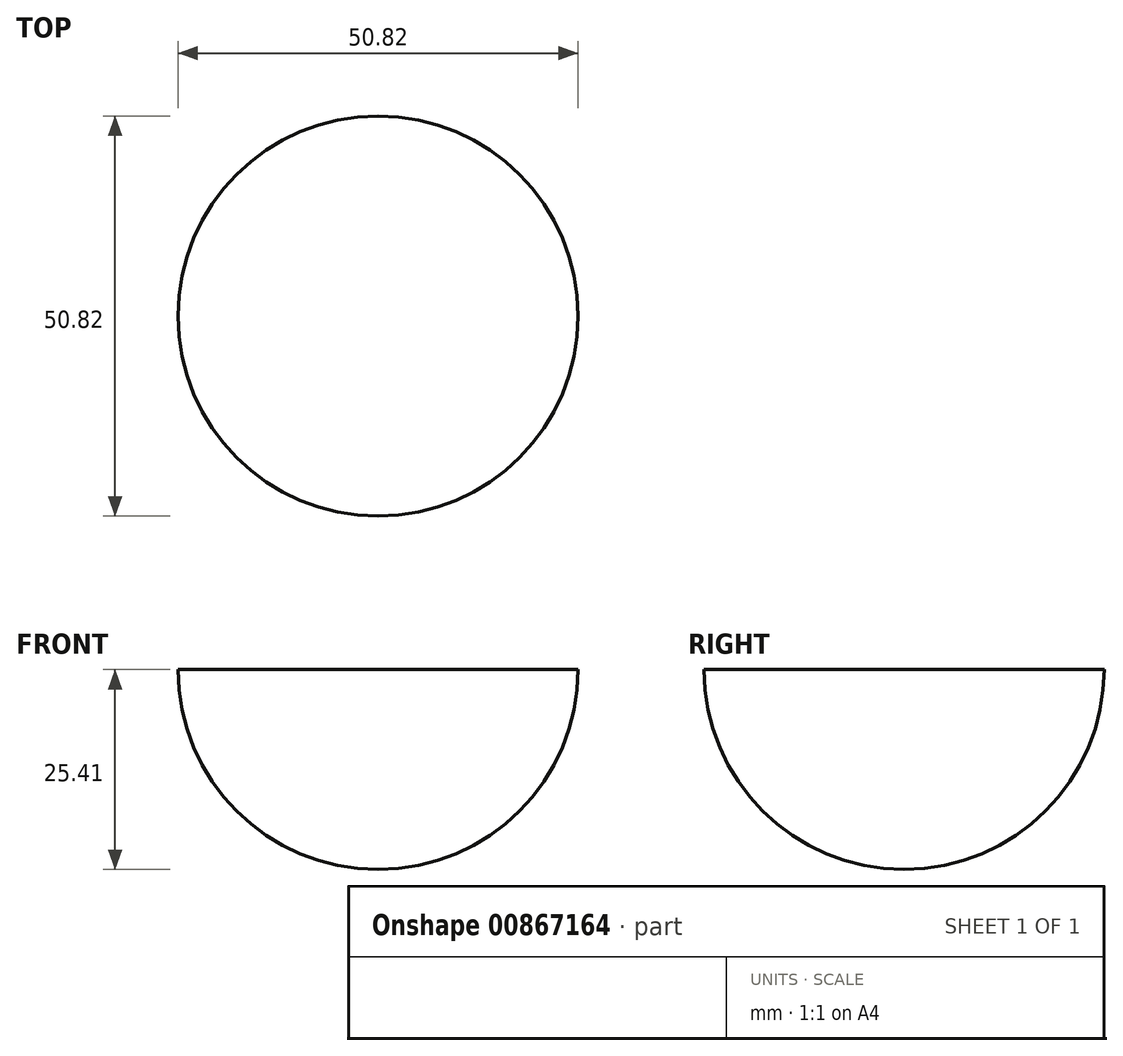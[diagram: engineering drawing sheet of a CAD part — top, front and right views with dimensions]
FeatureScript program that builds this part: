
annotation { "Feature Type Name" : "Feature", "Feature Type Description" : "" }
export const myFeature = defineFeature(function(context is Context, id is Id, definition is map)
    precondition{}
    {
        {
            var Q0;
            Q0=qCreatedBy(makeId("Top.planeOp"),FACE);
            var sketch = newSketch(context, id + "F0", { "sketchPlane" : qUnion([Q0])});
            skArc(sketch, "E0", {"start": v(0, -25.41) * mm, "mid": v(25.41, 0) * mm, "end": v(0, 25.41) * mm});
            skSolve(sketch);
        }
        {
            var Q0;
            Q0=qCreatedBy(makeId("Top.planeOp"),FACE);
            var sketch = newSketch(context, id + "F1", { "sketchPlane" : qUnion([Q0])});
            skLineSegment(sketch, "E1", {"start": v(0, 25.34) * mm, "end": v(0, 0) * mm});
            skSolve(sketch);
        }
        {
            var Q0;
            Q0=sQuery(id+"F0.wireOp",EDGE,"E0");
            var Q1;
            Q1=sQuery(id+"F1.wireOp",EDGE,"E1");
            revolve(context, id + "F2", {"bodyType" : ToolBodyType.SURFACE, "surfaceOperationType" : NewSurfaceOperationType.NEW, "surfaceEntities" : qUnion([Q0]), "axis" : qUnion([Q1]), "revolveType" : RevolveType.ONE_DIRECTION, "oppositeDirection" : true, "angle" : 180 * degree});
        }
    });
